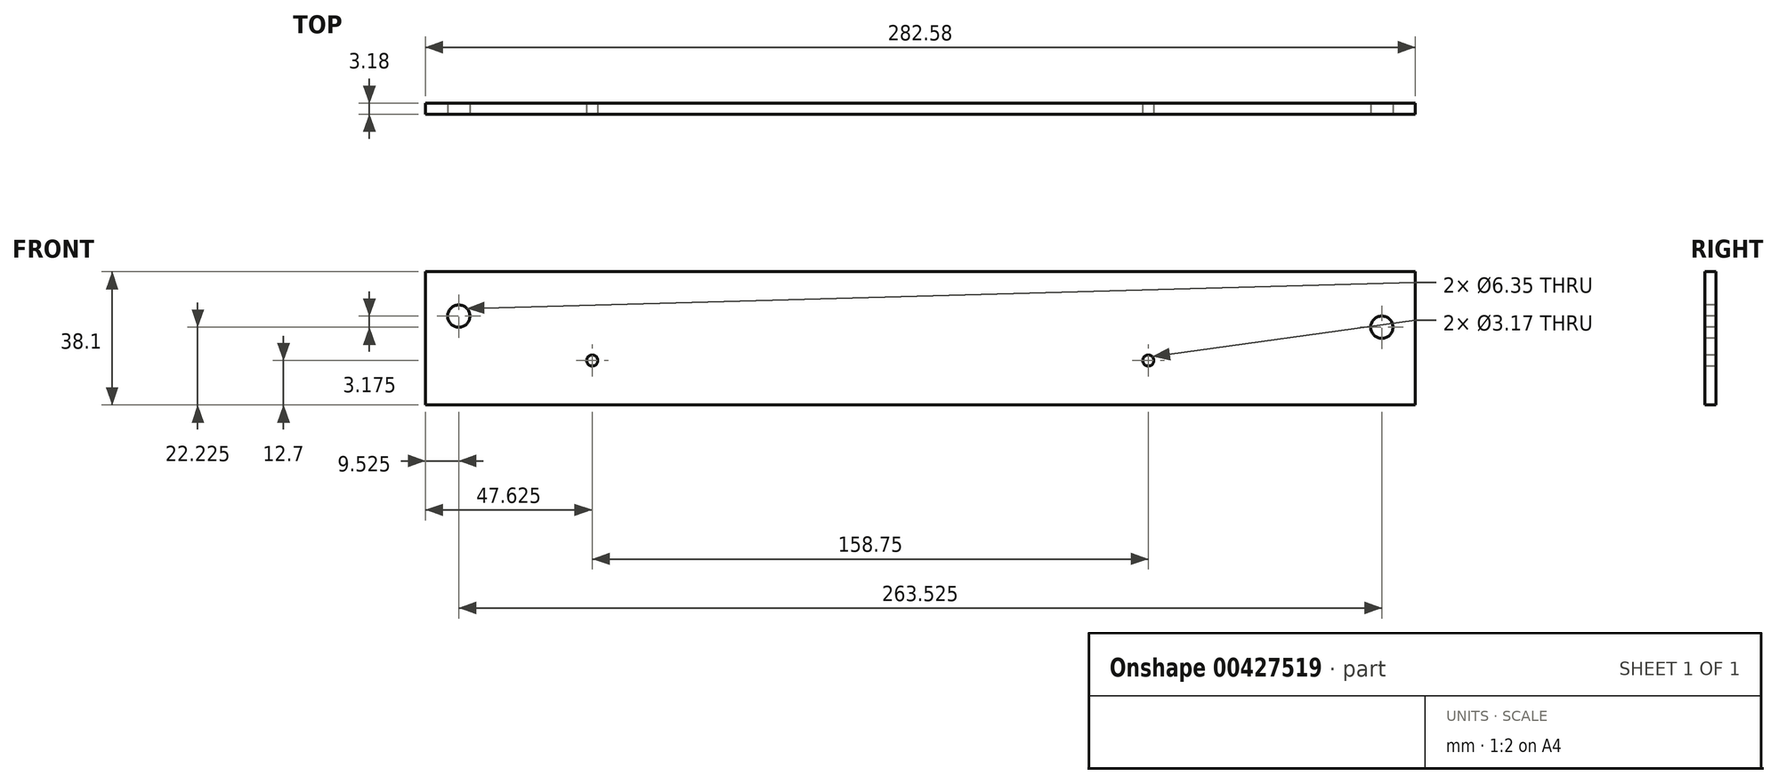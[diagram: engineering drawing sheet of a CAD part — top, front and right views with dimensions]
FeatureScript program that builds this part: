
annotation { "Feature Type Name" : "Feature", "Feature Type Description" : "" }
export const myFeature = defineFeature(function(context is Context, id is Id, definition is map)
    precondition{}
    {
        {
            var Q0;
            Q0=qCreatedBy(makeId("Front.planeOp"),FACE);
            var sketch = newSketch(context, id + "F0", { "sketchPlane" : qUnion([Q0])});
            skLineSegment(sketch, "E0.bottom", {"start": v(0, 0) * mm, "end": v(282.58, 0) * mm});
            skLineSegment(sketch, "E0.top", {"start": v(0, -38.1) * mm, "end": v(282.58, -38.1) * mm});
            skLineSegment(sketch, "E0.left", {"start": v(0, 0) * mm, "end": v(0, -38.1) * mm});
            skLineSegment(sketch, "E0.right", {"start": v(282.58, 0) * mm, "end": v(282.58, -38.1) * mm});
            skSolve(sketch);
        }
        {
            var Q0;
            Q0 = qSketchRegion(id + "F0", true);
            extrude(context, id + "F1", {"entities" : qUnion([Q0]), "oppositeDirection" : true, "depth" : 3.17 * mm});
        }
        {
            var Q0;
            Q0=qCreatedBy(makeId("Front.planeOp"),FACE);
            var sketch = newSketch(context, id + "F2", { "sketchPlane" : qUnion([Q0])});
            skCircle(sketch, "E1", {"center": v(9.52, -12.7) * mm, "radius": 3.18 * mm});
            skCircle(sketch, "E2", {"center": v(273.05, -15.88) * mm, "radius": 3.18 * mm});
            skCircle(sketch, "E3", {"center": v(47.63, -25.4) * mm, "radius": 1.59 * mm});
            skCircle(sketch, "E4.1.0.0", {"center": v(206.38, -25.4) * mm, "radius": 1.59 * mm});
            skLineSegment(sketch, "E4.direction1", {"start": v(47.62, -25.4) * mm, "end": v(206.38, -25.4) * mm, "construction": true});
            skSolve(sketch);
        }
        {
            var Q0;
            Q0 = qSketchRegion(id + "F2", true);
            extrude(context, id + "F3", {"entities" : qUnion([Q0]), "operationType" : NewBodyOperationType.REMOVE, "endBound" : BoundingType.THROUGH_ALL, "oppositeDirection" : true, "depth" : 25.4 * mm});
        }
    });
